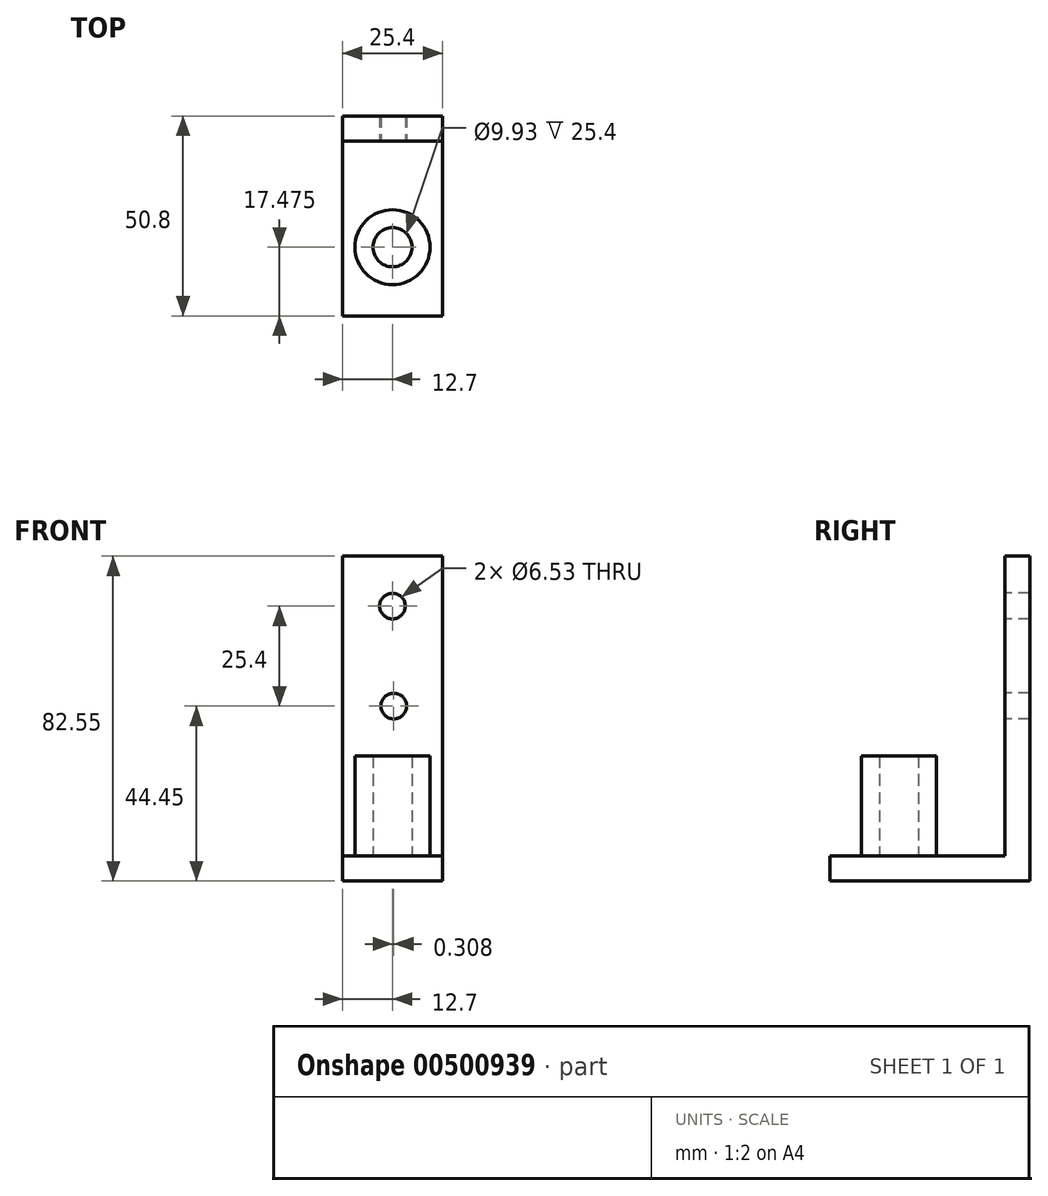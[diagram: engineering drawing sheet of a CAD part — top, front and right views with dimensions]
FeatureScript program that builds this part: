
annotation { "Feature Type Name" : "Feature", "Feature Type Description" : "" }
export const myFeature = defineFeature(function(context is Context, id is Id, definition is map)
    precondition{}
    {
        {
            var Q0;
            Q0=qCreatedBy(makeId("Right.planeOp"),FACE);
            var sketch = newSketch(context, id + "F0", { "sketchPlane" : qUnion([Q0])});
            skLineSegment(sketch, "E0", {"start": v(0, 0) * mm, "end": v(-50.8, 0) * mm});
            skLineSegment(sketch, "E1", {"start": v(-50.8, 0) * mm, "end": v(-50.8, 6.35) * mm});
            skLineSegment(sketch, "E2", {"start": v(-50.8, 6.35) * mm, "end": v(-6.35, 6.35) * mm});
            skLineSegment(sketch, "E3", {"start": v(-6.35, 6.35) * mm, "end": v(-6.35, 82.55) * mm});
            skLineSegment(sketch, "E4", {"start": v(-6.35, 82.55) * mm, "end": v(0, 82.55) * mm});
            skLineSegment(sketch, "E5", {"start": v(0, 82.55) * mm, "end": v(0, 0) * mm});
            skSolve(sketch);
        }
        {
            var Q0;
            Q0=makeQuery(id+"F0.imprint","IMPRINT",FACE,{"disambiguationData":[TD([[makeQuery(id+"F0.imprint","IMPRINT",EDGE,{"derivedFrom":sQuery(id+"F0.wireOp",EDGE,"E0")}),-1.0]])]});
            extrude(context, id + "F1", {"entities" : qUnion([Q0]), "depth" : 25.4 * mm, "offsetDistance" : 25.4 * mm});
        }
        {
            var Q0;
            Q0=makeQuery(id+"F1.opExtrude","SWEPT_FACE",FACE,{"disambiguationData":[OSD([sQuery(id+"F0.wireOp",EDGE,"E2")])]});
            var sketch = newSketch(context, id + "F2", { "sketchPlane" : qUnion([Q0])});
            skCircle(sketch, "E6", {"center": v(12.7, -33.32) * mm, "radius": 4.97 * mm});
            skCircle(sketch, "E7", {"center": v(12.7, -33.32) * mm, "radius": 9.53 * mm});
            skSolve(sketch);
        }
        {
            var Q0;
            Q0=makeQuery(id+"F2.imprint","IMPRINT",FACE,{"disambiguationData":[TD([[makeQuery(id+"F2.imprint","IMPRINT",EDGE,{"derivedFrom":sQuery(id+"F2.wireOp",EDGE,"E6")}),-1.0]])]});
            extrude(context, id + "F3", {"entities" : qUnion([Q0]), "operationType" : NewBodyOperationType.ADD, "depth" : 25.4 * mm, "offsetDistance" : 25.4 * mm});
        }
        {
            var Q0;
            Q0=makeQuery(id+"F1.opExtrude","SWEPT_FACE",FACE,{"disambiguationData":[OSD([sQuery(id+"F0.wireOp",EDGE,"E3")])]});
            var sketch = newSketch(context, id + "F4", { "sketchPlane" : qUnion([Q0])});
            skCircle(sketch, "E8", {"center": v(12.7, 69.85) * mm, "radius": 3.26 * mm});
            skCircle(sketch, "E9", {"center": v(13, 44.45) * mm, "radius": 3.26 * mm});
            skSolve(sketch);
        }
        {
            var Q0;
            Q0=makeQuery(id+"F4.imprint","IMPRINT",FACE,{"disambiguationData":[TD([[makeQuery(id+"F4.imprint","IMPRINT",EDGE,{"derivedFrom":sQuery(id+"F4.wireOp",EDGE,"E8")}),1.0]])]});
            var Q1;
            Q1=makeQuery(id+"F4.imprint","IMPRINT",FACE,{"disambiguationData":[TD([[makeQuery(id+"F4.imprint","IMPRINT",EDGE,{"derivedFrom":sQuery(id+"F4.wireOp",EDGE,"E9")}),1.0]])]});
            extrude(context, id + "F5", {"entities" : qUnion([Q0, Q1]), "operationType" : NewBodyOperationType.REMOVE, "oppositeDirection" : true, "depth" : 25.4 * mm, "offsetDistance" : 25.4 * mm});
        }
    });
